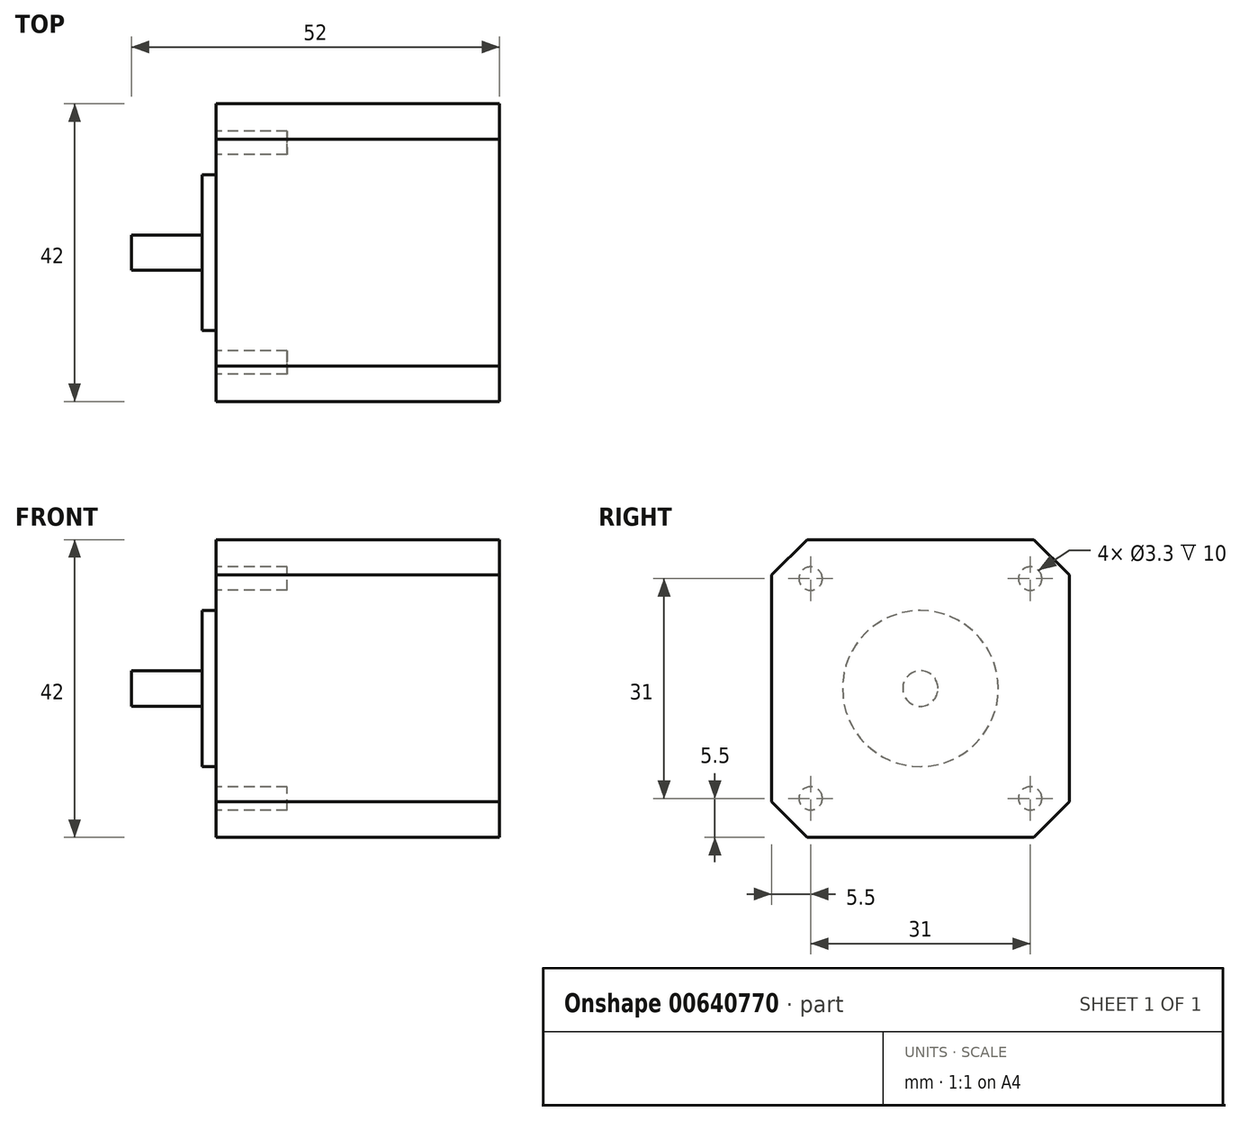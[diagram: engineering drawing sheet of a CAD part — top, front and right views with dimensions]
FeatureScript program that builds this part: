
annotation { "Feature Type Name" : "Feature", "Feature Type Description" : "" }
export const myFeature = defineFeature(function(context is Context, id is Id, definition is map)
    precondition{}
    {
        {
            var Q0;
            Q0=qCreatedBy(makeId("Right.planeOp"),FACE);
            var sketch = newSketch(context, id + "F0", { "sketchPlane" : qUnion([Q0])});
            skLineSegment(sketch, "E0.bottom", {"start": v(-21, 21) * mm, "end": v(21, 21) * mm});
            skLineSegment(sketch, "E0.top", {"start": v(-21, -21) * mm, "end": v(21, -21) * mm});
            skLineSegment(sketch, "E0.left", {"start": v(-21, 21) * mm, "end": v(-21, -21) * mm});
            skLineSegment(sketch, "E0.right", {"start": v(21, 21) * mm, "end": v(21, -21) * mm});
            skPoint(sketch, "E0.middle", {"position": v(0, 0) * mm});
            skLineSegment(sketch, "E1.bottom", {"start": v(-15.5, 15.5) * mm, "end": v(15.5, 15.5) * mm, "construction": true});
            skLineSegment(sketch, "E1.top", {"start": v(-15.5, -15.5) * mm, "end": v(15.5, -15.5) * mm, "construction": true});
            skLineSegment(sketch, "E1.left", {"start": v(-15.5, 15.5) * mm, "end": v(-15.5, -15.5) * mm, "construction": true});
            skLineSegment(sketch, "E1.right", {"start": v(15.5, 15.5) * mm, "end": v(15.5, -15.5) * mm, "construction": true});
            skCircle(sketch, "E2", {"center": v(-15.5, 15.5) * mm, "radius": 1.65 * mm});
            skCircle(sketch, "E3", {"center": v(15.5, 15.5) * mm, "radius": 1.65 * mm});
            skCircle(sketch, "E4", {"center": v(15.5, -15.5) * mm, "radius": 1.65 * mm});
            skCircle(sketch, "E5", {"center": v(-15.5, -15.5) * mm, "radius": 1.65 * mm});
            skCircle(sketch, "E6", {"center": v(0, 0) * mm, "radius": 11 * mm});
            skCircle(sketch, "E7", {"center": v(0, 0) * mm, "radius": 2.5 * mm});
            skSolve(sketch);
        }
        {
            var Q0;
            Q0=makeQuery(id+"F0.imprint","IMPRINT",FACE,{"disambiguationData":[TD([[makeQuery(id+"F0.imprint","IMPRINT",EDGE,{"derivedFrom":sQuery(id+"F0.wireOp",EDGE,"E0.bottom")}),-1.0]])]});
            var Q1;
            Q1=makeQuery(id+"F0.imprint","IMPRINT",FACE,{"disambiguationData":[TD([[makeQuery(id+"F0.imprint","IMPRINT",EDGE,{"derivedFrom":sQuery(id+"F0.wireOp",EDGE,"E4")}),1.0]])]});
            var Q2;
            Q2=makeQuery(id+"F0.imprint","IMPRINT",FACE,{"disambiguationData":[TD([[makeQuery(id+"F0.imprint","IMPRINT",EDGE,{"derivedFrom":sQuery(id+"F0.wireOp",EDGE,"E5")}),1.0]])]});
            var Q3;
            Q3=makeQuery(id+"F0.imprint","IMPRINT",FACE,{"disambiguationData":[TD([[makeQuery(id+"F0.imprint","IMPRINT",EDGE,{"derivedFrom":sQuery(id+"F0.wireOp",EDGE,"E2")}),1.0]])]});
            var Q4;
            Q4=makeQuery(id+"F0.imprint","IMPRINT",FACE,{"disambiguationData":[TD([[makeQuery(id+"F0.imprint","IMPRINT",EDGE,{"derivedFrom":sQuery(id+"F0.wireOp",EDGE,"E3")}),1.0]])]});
            var Q5;
            Q5=makeQuery(id+"F0.imprint","IMPRINT",FACE,{"disambiguationData":[TD([[makeQuery(id+"F0.imprint","IMPRINT",EDGE,{"derivedFrom":sQuery(id+"F0.wireOp",EDGE,"E6")}),1.0]])]});
            var Q6;
            Q6=makeQuery(id+"F0.imprint","IMPRINT",FACE,{"disambiguationData":[TD([[makeQuery(id+"F0.imprint","IMPRINT",EDGE,{"derivedFrom":sQuery(id+"F0.wireOp",EDGE,"E7")}),1.0]])]});
            extrude(context, id + "F1", {"entities" : qUnion([Q0, Q1, Q2, Q3, Q4, Q5, Q6]), "depth" : 40 * mm, "offsetDistance" : 25 * mm});
        }
        {
            var Q0;
            Q0=makeQuery(id+"F0.imprint","IMPRINT",FACE,{"disambiguationData":[TD([[makeQuery(id+"F0.imprint","IMPRINT",EDGE,{"derivedFrom":sQuery(id+"F0.wireOp",EDGE,"E6")}),1.0]])]});
            var Q1;
            Q1=makeQuery(id+"F0.imprint","IMPRINT",FACE,{"disambiguationData":[TD([[makeQuery(id+"F0.imprint","IMPRINT",EDGE,{"derivedFrom":sQuery(id+"F0.wireOp",EDGE,"E7")}),1.0]])]});
            extrude(context, id + "F2", {"entities" : qUnion([Q0, Q1]), "operationType" : NewBodyOperationType.ADD, "oppositeDirection" : true, "depth" : 2 * mm, "offsetDistance" : 25 * mm});
        }
        {
            var Q0;
            Q0=makeQuery(id+"F0.imprint","IMPRINT",FACE,{"disambiguationData":[TD([[makeQuery(id+"F0.imprint","IMPRINT",EDGE,{"derivedFrom":sQuery(id+"F0.wireOp",EDGE,"E7")}),1.0]])]});
            extrude(context, id + "F3", {"entities" : qUnion([Q0]), "operationType" : NewBodyOperationType.ADD, "oppositeDirection" : true, "depth" : 12 * mm, "offsetDistance" : 25 * mm});
        }
        {
            var Q0;
            Q0=makeQuery(id+"F0.imprint","IMPRINT",FACE,{"disambiguationData":[TD([[makeQuery(id+"F0.imprint","IMPRINT",EDGE,{"derivedFrom":sQuery(id+"F0.wireOp",EDGE,"E3")}),1.0]])]});
            var Q1;
            Q1=makeQuery(id+"F0.imprint","IMPRINT",FACE,{"disambiguationData":[TD([[makeQuery(id+"F0.imprint","IMPRINT",EDGE,{"derivedFrom":sQuery(id+"F0.wireOp",EDGE,"E4")}),1.0]])]});
            var Q2;
            Q2=makeQuery(id+"F0.imprint","IMPRINT",FACE,{"disambiguationData":[TD([[makeQuery(id+"F0.imprint","IMPRINT",EDGE,{"derivedFrom":sQuery(id+"F0.wireOp",EDGE,"E2")}),1.0]])]});
            var Q3;
            Q3=makeQuery(id+"F0.imprint","IMPRINT",FACE,{"disambiguationData":[TD([[makeQuery(id+"F0.imprint","IMPRINT",EDGE,{"derivedFrom":sQuery(id+"F0.wireOp",EDGE,"E5")}),1.0]])]});
            extrude(context, id + "F4", {"entities" : qUnion([Q0, Q1, Q2, Q3]), "operationType" : NewBodyOperationType.REMOVE, "depth" : 10 * mm, "offsetDistance" : 25 * mm});
        }
        {
            var Q0;
            Q0=makeQuery(id+"F1.opExtrude","SWEPT_EDGE",EDGE,{"disambiguationData":[OSD([sQuery(id+"F0.wireOp",EDGE,"E0.bottom"),sQuery(id+"F0.wireOp",EDGE,"E0.left")])]});
            var Q1;
            Q1=makeQuery(id+"F1.opExtrude","SWEPT_EDGE",EDGE,{"disambiguationData":[OSD([sQuery(id+"F0.wireOp",EDGE,"E0.bottom"),sQuery(id+"F0.wireOp",EDGE,"E0.right")])]});
            var Q2;
            Q2=makeQuery(id+"F1.opExtrude","SWEPT_EDGE",EDGE,{"disambiguationData":[OSD([sQuery(id+"F0.wireOp",EDGE,"E0.top"),sQuery(id+"F0.wireOp",EDGE,"E0.right")])]});
            var Q3;
            Q3=makeQuery(id+"F1.opExtrude","SWEPT_EDGE",EDGE,{"disambiguationData":[OSD([sQuery(id+"F0.wireOp",EDGE,"E0.top"),sQuery(id+"F0.wireOp",EDGE,"E0.left")])]});
            chamfer(context, id + "F5", {"entities" : qUnion([Q0, Q1, Q2, Q3]), "width" : 5 * mm, "tangentPropagation" : true});
        }
    });
